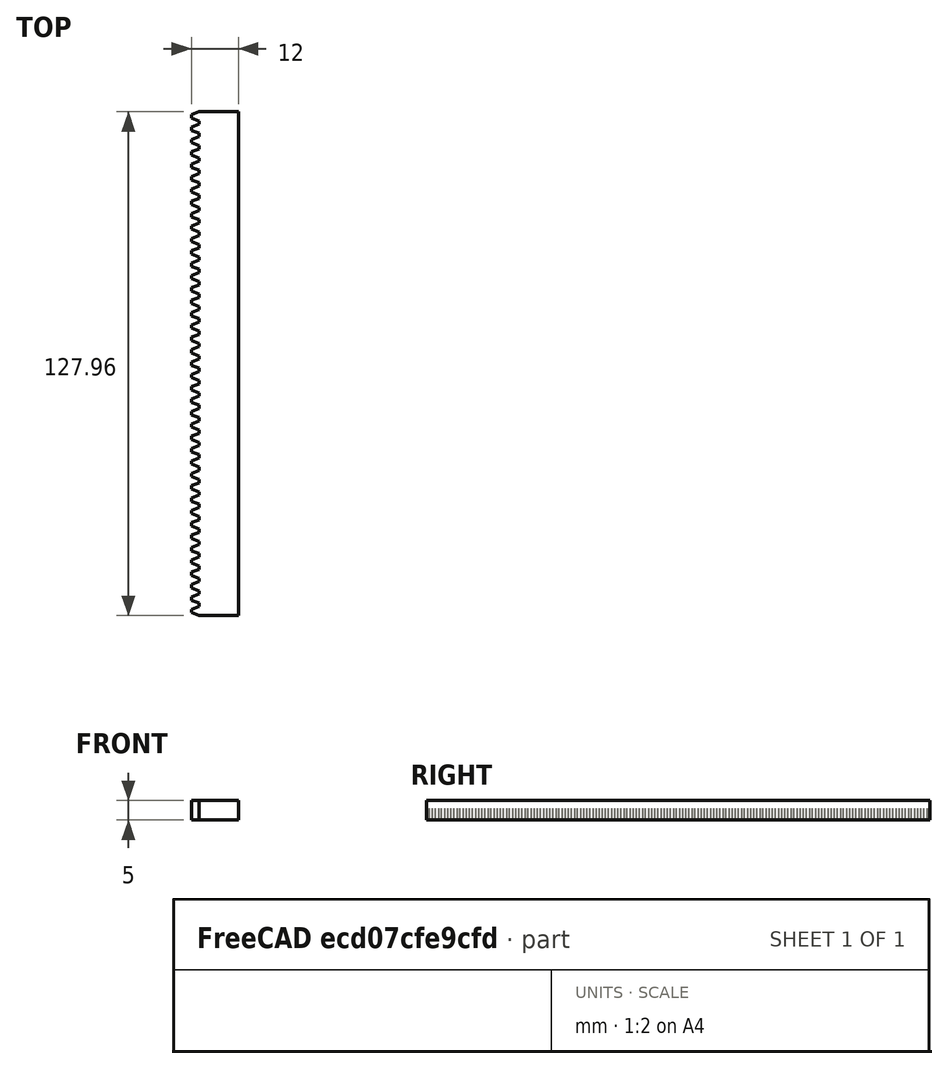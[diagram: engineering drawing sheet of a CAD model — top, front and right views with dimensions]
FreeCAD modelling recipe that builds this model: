
FCSTD DOCUMENT  (FreeCAD 0.16RUnknown)
Label: L130
License: All rights reserved
LicenseURL: http://en.wikipedia.org/wiki/All_rights_reserved
objects: Part::FeaturePython×1, Sketcher::SketchObject×1, PartDesign::Pocket×1, PartDesign::LinearPattern×1
note: 5 computed .brp shape members not serialized (recipe doc carries the construction recipe); baked Part::Feature solids carry a one-line shape summary decoded from their .brp

FEATURE [Part::FeaturePython] InvoluteRack  # WARN: FeaturePython — macro-defined, semantics opaque (R4)
  height = 5
  module = 1
  pressure_angle = 20
  teeth = 40
  thickness = 10
FEATURE [Sketcher::SketchObject] Sketch
  Placement = pos=(0,0,0) rot=(1,0,0;3.14159rad)
  Support = -> InvoluteRack [Face167]
  sketch-geometry (1):
    g0: Circle CenterX=6 CenterY=-3.18299 CenterZ=0 NormalX=0 NormalY=0 NormalZ=1 Radius=2.05
  constraints (2):
    c: Radius(g0) = 2.05
    c: DistanceX(g0) = 6
FEATURE [PartDesign::Pocket] Pocket
  Length = 5
  Sketch = -> Sketch
  Type = 1
FEATURE [PartDesign::LinearPattern] LinearPattern
  Direction = -> Sketch [V_Axis]
  Length = 120
  Occurrences = 11
  Originals = -> [Pocket]
  Reversed = true
